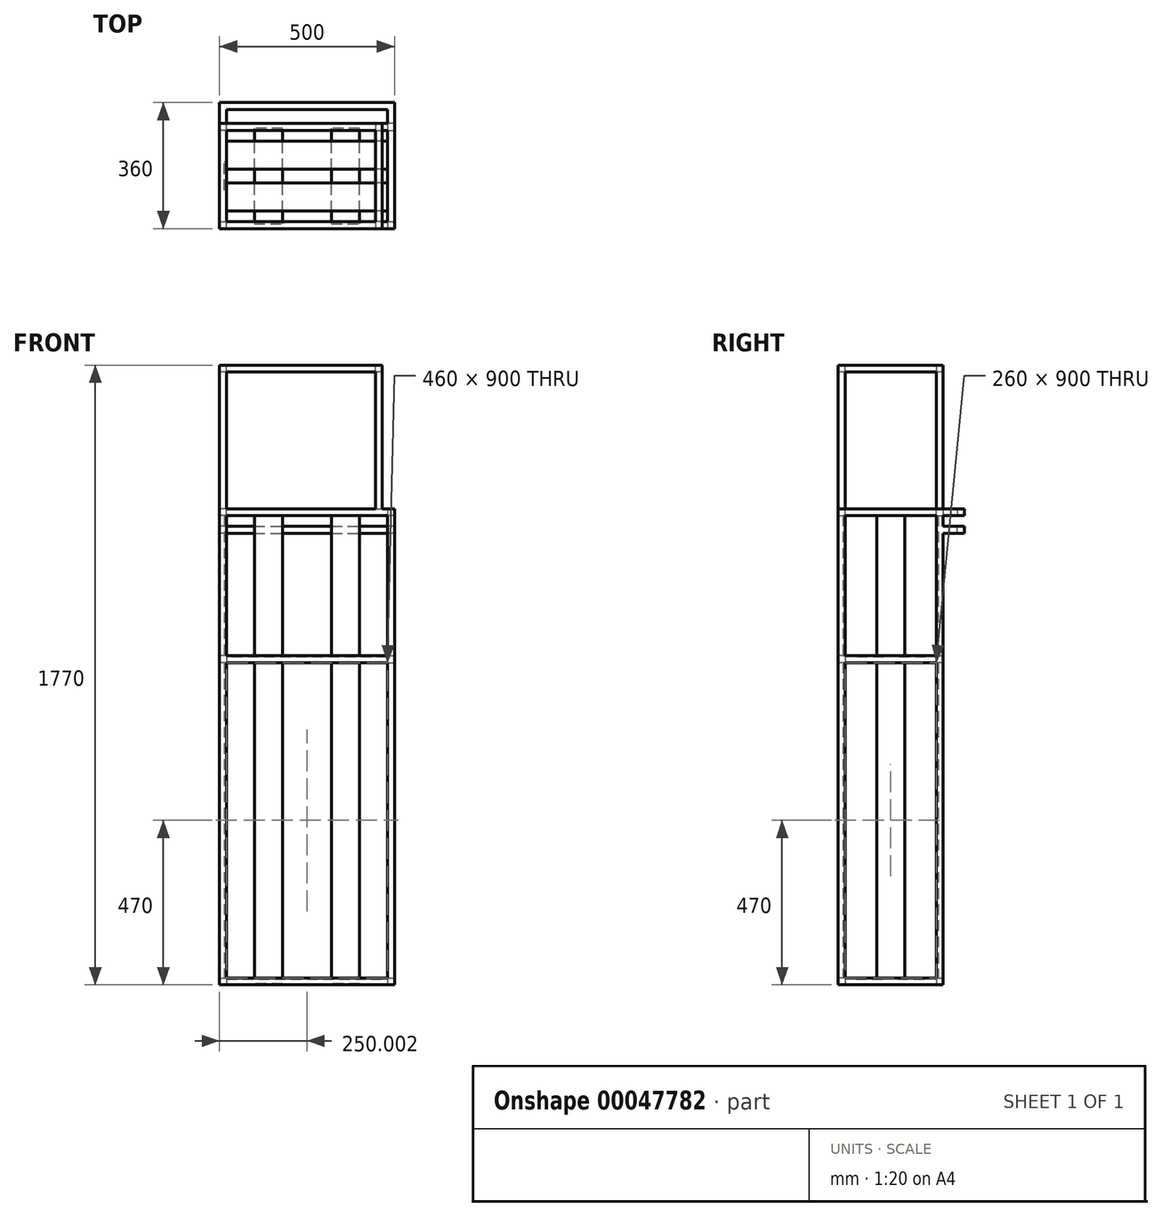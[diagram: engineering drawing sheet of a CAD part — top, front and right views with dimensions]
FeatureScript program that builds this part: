
annotation { "Feature Type Name" : "Feature", "Feature Type Description" : "" }
export const myFeature = defineFeature(function(context is Context, id is Id, definition is map)
    precondition{}
    {
        {
            var Q0;
            Q0=qCreatedBy(makeId("Top.planeOp"),FACE);
            var sketch = newSketch(context, id + "F0", { "sketchPlane" : qUnion([Q0])});
            skLineSegment(sketch, "E0.bottom", {"start": v(-269.64, 126.7) * mm, "end": v(230.36, 126.7) * mm});
            skLineSegment(sketch, "E0.top", {"start": v(-269.64, -173.3) * mm, "end": v(230.36, -173.3) * mm});
            skLineSegment(sketch, "E0.left", {"start": v(-269.64, 126.7) * mm, "end": v(-269.64, -173.3) * mm});
            skLineSegment(sketch, "E0.right", {"start": v(230.36, 126.7) * mm, "end": v(230.36, -173.3) * mm});
            skLineSegment(sketch, "E1.bottom", {"start": v(-249.64, 106.7) * mm, "end": v(210.36, 106.7) * mm});
            skLineSegment(sketch, "E1.top", {"start": v(-249.64, -153.3) * mm, "end": v(210.36, -153.3) * mm});
            skLineSegment(sketch, "E1.left", {"start": v(-249.64, 106.7) * mm, "end": v(-249.64, -153.3) * mm});
            skLineSegment(sketch, "E1.right", {"start": v(210.36, 106.7) * mm, "end": v(210.36, -153.3) * mm});
            skSolve(sketch);
        }
        {
            var Q0;
            Q0=makeQuery(id+"F0.imprint","IMPRINT",FACE,{"disambiguationData":[TD([[makeQuery(id+"F0.imprint","IMPRINT",EDGE,{"derivedFrom":sQuery(id+"F0.wireOp",EDGE,"E0.bottom")}),-1.0]])]});
            extrude(context, id + "F1", {"entities" : qUnion([Q0]), "depth" : 20 * mm});
        }
        {
            var Q0;
            Q0=makeQuery(id+"F1.opExtrude","SWEPT_FACE",FACE,{"disambiguationData":[OSD([sQuery(id+"F0.wireOp",EDGE,"E1.bottom")])]});
            var sketch = newSketch(context, id + "F2", { "sketchPlane" : qUnion([Q0])});
            skLineSegment(sketch, "E2.bottom", {"start": v(-169.64, 0) * mm, "end": v(-89.64, 0) * mm});
            skLineSegment(sketch, "E2.top", {"start": v(-169.64, 3) * mm, "end": v(-89.64, 3) * mm});
            skLineSegment(sketch, "E2.left", {"start": v(-169.64, 0) * mm, "end": v(-169.64, 3) * mm});
            skLineSegment(sketch, "E2.right", {"start": v(-89.64, 0) * mm, "end": v(-89.64, 3) * mm});
            skLineSegment(sketch, "E3.bottom", {"start": v(50.36, 3) * mm, "end": v(130.36, 3) * mm});
            skLineSegment(sketch, "E3.top", {"start": v(50.36, 0) * mm, "end": v(130.36, 0) * mm});
            skLineSegment(sketch, "E3.left", {"start": v(50.36, 3) * mm, "end": v(50.36, 0) * mm});
            skLineSegment(sketch, "E3.right", {"start": v(130.36, 3) * mm, "end": v(130.36, 0) * mm});
            skSolve(sketch);
        }
        {
            var Q0;
            Q0 = qSketchRegion(id + "F2", true);
            extrude(context, id + "F3", {"entities" : qUnion([Q0]), "operationType" : NewBodyOperationType.ADD, "endBound" : BoundingType.UP_TO_NEXT, "depth" : 25 * mm});
        }
        {
            var Q0;
            Q0=makeQuery(id+"F1.opExtrude","SWEPT_FACE",FACE,{"disambiguationData":[OSD([sQuery(id+"F0.wireOp",EDGE,"E1.right")])]});
            var sketch = newSketch(context, id + "F4", { "sketchPlane" : qUnion([Q0])});
            skLineSegment(sketch, "E4.bottom", {"start": v(-76.7, 20) * mm, "end": v(3.3, 20) * mm});
            skLineSegment(sketch, "E4.top", {"start": v(-76.7, 17) * mm, "end": v(3.3, 17) * mm});
            skLineSegment(sketch, "E4.left", {"start": v(-76.7, 20) * mm, "end": v(-76.7, 17) * mm});
            skLineSegment(sketch, "E4.right", {"start": v(3.3, 20) * mm, "end": v(3.3, 17) * mm});
            skLineSegment(sketch, "E5.bottom", {"start": v(43.3, 20) * mm, "end": v(123.3, 20) * mm});
            skLineSegment(sketch, "E5.top", {"start": v(43.3, 17) * mm, "end": v(123.3, 17) * mm});
            skLineSegment(sketch, "E5.left", {"start": v(43.3, 20) * mm, "end": v(43.3, 17) * mm});
            skLineSegment(sketch, "E5.right", {"start": v(123.3, 20) * mm, "end": v(123.3, 17) * mm});
            skSolve(sketch);
        }
        {
            var Q0;
            Q0 = qSketchRegion(id + "F4", true);
            extrude(context, id + "F5", {"entities" : qUnion([Q0]), "operationType" : NewBodyOperationType.ADD, "endBound" : BoundingType.UP_TO_NEXT, "depth" : 25 * mm});
        }
        {
            var Q0;
            Q0=makeQuery(id+"F5.boolean.opBoolean","MERGE",FACE,{"derivedFrom":[makeQuery(id+"F1.opExtrude","CAP_FACE",FACE,{"disambiguationData":[OSD([sQuery(id+"F0.wireOp",EDGE,"E0.bottom"),sQuery(id+"F0.wireOp",EDGE,"E0.top"),sQuery(id+"F0.wireOp",EDGE,"E0.left"),sQuery(id+"F0.wireOp",EDGE,"E0.right"),sQuery(id+"F0.wireOp",EDGE,"E1.bottom"),sQuery(id+"F0.wireOp",EDGE,"E1.top"),sQuery(id+"F0.wireOp",EDGE,"E1.left"),sQuery(id+"F0.wireOp",EDGE,"E1.right")])],"isStart":false}),makeQuery(id+"F5.opExtrude","SWEPT_FACE",FACE,{"disambiguationData":[OSD([sQuery(id+"F4.wireOp",EDGE,"E4.bottom")])]}),makeQuery(id+"F5.opExtrude","SWEPT_FACE",FACE,{"disambiguationData":[OSD([sQuery(id+"F4.wireOp",EDGE,"E5.bottom")])]})]});
            var sketch = newSketch(context, id + "F6", { "sketchPlane" : qUnion([Q0])});
            skLineSegment(sketch, "E6.bottom", {"start": v(-269.64, 126.7) * mm, "end": v(-249.64, 126.7) * mm});
            skLineSegment(sketch, "E6.top", {"start": v(-269.64, 106.7) * mm, "end": v(-249.64, 106.7) * mm});
            skLineSegment(sketch, "E6.left", {"start": v(-269.64, 126.7) * mm, "end": v(-269.64, 106.7) * mm});
            skLineSegment(sketch, "E6.right", {"start": v(-249.64, 126.7) * mm, "end": v(-249.64, 106.7) * mm});
            skLineSegment(sketch, "E7.bottom", {"start": v(-269.64, -173.3) * mm, "end": v(-249.64, -173.3) * mm});
            skLineSegment(sketch, "E7.top", {"start": v(-269.64, -153.3) * mm, "end": v(-249.64, -153.3) * mm});
            skLineSegment(sketch, "E7.left", {"start": v(-269.64, -173.3) * mm, "end": v(-269.64, -153.3) * mm});
            skLineSegment(sketch, "E7.right", {"start": v(-249.64, -173.3) * mm, "end": v(-249.64, -153.3) * mm});
            skLineSegment(sketch, "E8.bottom", {"start": v(210.36, -153.3) * mm, "end": v(230.36, -153.3) * mm});
            skLineSegment(sketch, "E8.top", {"start": v(210.36, -173.3) * mm, "end": v(230.36, -173.3) * mm});
            skLineSegment(sketch, "E8.left", {"start": v(210.36, -153.3) * mm, "end": v(210.36, -173.3) * mm});
            skLineSegment(sketch, "E8.right", {"start": v(230.36, -153.3) * mm, "end": v(230.36, -173.3) * mm});
            skLineSegment(sketch, "E9.bottom", {"start": v(210.36, 106.7) * mm, "end": v(230.36, 106.7) * mm});
            skLineSegment(sketch, "E9.top", {"start": v(210.36, 126.7) * mm, "end": v(230.36, 126.7) * mm});
            skLineSegment(sketch, "E9.left", {"start": v(210.36, 106.7) * mm, "end": v(210.36, 126.7) * mm});
            skLineSegment(sketch, "E9.right", {"start": v(230.36, 106.7) * mm, "end": v(230.36, 126.7) * mm});
            skSolve(sketch);
        }
        {
            var Q0;
            Q0 = qSketchRegion(id + "F6", true);
            extrude(context, id + "F7", {"entities" : qUnion([Q0]), "operationType" : NewBodyOperationType.ADD, "depth" : 1340 * mm});
        }
        {
            var Q0;
            Q0=makeQuery(id+"F7.opExtrude","SWEPT_FACE",FACE,{"disambiguationData":[OSD([sQuery(id+"F6.wireOp",EDGE,"E8.left")])]});
            var sketch = newSketch(context, id + "F8", { "sketchPlane" : qUnion([Q0])});
            skLineSegment(sketch, "E10.bottom", {"start": v(153.3, 920) * mm, "end": v(173.3, 920) * mm});
            skLineSegment(sketch, "E10.top", {"start": v(153.3, 940) * mm, "end": v(173.3, 940) * mm});
            skLineSegment(sketch, "E10.left", {"start": v(153.3, 940) * mm, "end": v(153.3, 920) * mm});
            skLineSegment(sketch, "E10.right", {"start": v(173.3, 940) * mm, "end": v(173.3, 920) * mm});
            skSolve(sketch);
        }
        {
            var Q0;
            Q0 = qSketchRegion(id + "F8", true);
            extrude(context, id + "F9", {"entities" : qUnion([Q0]), "operationType" : NewBodyOperationType.ADD, "endBound" : BoundingType.UP_TO_NEXT, "depth" : 25 * mm});
        }
        {
            var Q0;
            Q0=makeQuery(id+"F9.boolean.opBoolean","MERGE",FACE,{"derivedFrom":[makeQuery(id+"F7.opExtrude","SWEPT_FACE",FACE,{"disambiguationData":[OSD([sQuery(id+"F6.wireOp",EDGE,"E7.top")])]}),makeQuery(id+"F7.opExtrude","SWEPT_FACE",FACE,{"disambiguationData":[OSD([sQuery(id+"F6.wireOp",EDGE,"E8.bottom")])]}),makeQuery(id+"F9.opExtrude","SWEPT_FACE",FACE,{"disambiguationData":[OSD([sQuery(id+"F8.wireOp",EDGE,"E10.left")])]})]});
            var sketch = newSketch(context, id + "F10", { "sketchPlane" : qUnion([Q0])});
            skLineSegment(sketch, "E11.bottom", {"start": v(249.64, 940) * mm, "end": v(269.64, 940) * mm});
            skLineSegment(sketch, "E11.top", {"start": v(249.64, 920) * mm, "end": v(269.64, 920) * mm});
            skLineSegment(sketch, "E11.left", {"start": v(249.64, 940) * mm, "end": v(249.64, 920) * mm});
            skLineSegment(sketch, "E11.right", {"start": v(269.64, 940) * mm, "end": v(269.64, 920) * mm});
            skLineSegment(sketch, "E12.bottom", {"start": v(-210.36, 940) * mm, "end": v(-230.36, 940) * mm});
            skLineSegment(sketch, "E12.top", {"start": v(-210.36, 920) * mm, "end": v(-230.36, 920) * mm});
            skLineSegment(sketch, "E12.left", {"start": v(-210.36, 940) * mm, "end": v(-210.36, 920) * mm});
            skLineSegment(sketch, "E12.right", {"start": v(-230.36, 940) * mm, "end": v(-230.36, 920) * mm});
            skSolve(sketch);
        }
        {
            var Q0;
            Q0 = qSketchRegion(id + "F10", true);
            extrude(context, id + "F11", {"entities" : qUnion([Q0]), "operationType" : NewBodyOperationType.ADD, "endBound" : BoundingType.UP_TO_NEXT, "depth" : 25 * mm});
        }
        {
            var Q0;
            Q0=makeQuery(id+"F11.boolean.opBoolean","MERGE",FACE,{"derivedFrom":[makeQuery(id+"F7.opExtrude","SWEPT_FACE",FACE,{"disambiguationData":[OSD([sQuery(id+"F6.wireOp",EDGE,"E6.right")])]}),makeQuery(id+"F11.opExtrude","SWEPT_FACE",FACE,{"disambiguationData":[OSD([sQuery(id+"F10.wireOp",EDGE,"E11.left")])]})]});
            var sketch = newSketch(context, id + "F12", { "sketchPlane" : qUnion([Q0])});
            skLineSegment(sketch, "E13.bottom", {"start": v(106.7, 940) * mm, "end": v(126.7, 940) * mm});
            skLineSegment(sketch, "E13.top", {"start": v(106.7, 920) * mm, "end": v(126.7, 920) * mm});
            skLineSegment(sketch, "E13.left", {"start": v(106.7, 940) * mm, "end": v(106.7, 920) * mm});
            skLineSegment(sketch, "E13.right", {"start": v(126.7, 940) * mm, "end": v(126.7, 920) * mm});
            skSolve(sketch);
        }
        {
            var Q0;
            Q0 = qSketchRegion(id + "F12", true);
            extrude(context, id + "F13", {"entities" : qUnion([Q0]), "operationType" : NewBodyOperationType.ADD, "endBound" : BoundingType.UP_TO_NEXT, "depth" : 25 * mm});
        }
        {
            var Q0;
            {var subQ0=sQuery(id+"F0.wireOp",EDGE,"E0.left");var subQ1=sQuery(id+"F0.wireOp",EDGE,"E0.right");var subQ2=sQuery(id+"F0.wireOp",EDGE,"E1.bottom");var subQ3=sQuery(id+"F0.wireOp",EDGE,"E1.top");var subQ4=sQuery(id+"F0.wireOp",EDGE,"E1.left");var subQ5=sQuery(id+"F0.wireOp",EDGE,"E1.right");var subQ6=makeQuery(id+"F1.opExtrude","CAP_FACE",FACE,{"disambiguationData":[OSD([sQuery(id+"F0.wireOp",EDGE,"E0.bottom"),sQuery(id+"F0.wireOp",EDGE,"E0.top"),subQ0,subQ1,subQ2,subQ3,subQ4,subQ5])],"isStart":false});var subQ7=makeQuery(id+"F5.opExtrude","SWEPT_FACE",FACE,{"disambiguationData":[OSD([sQuery(id+"F4.wireOp",EDGE,"E4.bottom")])]});var subQ8=makeQuery(id+"F5.opExtrude","SWEPT_FACE",FACE,{"disambiguationData":[OSD([sQuery(id+"F4.wireOp",EDGE,"E5.bottom")])]});Q0=makeQuery(id+"F7.boolean.opBoolean","SPLIT",FACE,{"disambiguationData":[TD([makeQuery(id+"F1.opExtrude","SWEPT_FACE",FACE,{"disambiguationData":[OSD([subQ0])]})])],"derivedFrom":makeQuery(id+"F5.boolean.opBoolean","MERGE",FACE,{"derivedFrom":[subQ6,subQ7,subQ8]})});}
            var sketch = newSketch(context, id + "F14", { "sketchPlane" : qUnion([Q0])});
            skPoint(sketch, "E14", {"position": v(-269.64, -23.3) * mm});
            skLineSegment(sketch, "E15.bottom", {"start": v(-252.64, -63.3) * mm, "end": v(-255.64, -63.3) * mm});
            skLineSegment(sketch, "E15.top", {"start": v(-252.64, 16.7) * mm, "end": v(-255.64, 16.7) * mm});
            skLineSegment(sketch, "E15.left", {"start": v(-252.64, -63.3) * mm, "end": v(-252.64, 16.7) * mm});
            skLineSegment(sketch, "E15.right", {"start": v(-255.64, -63.3) * mm, "end": v(-255.64, 16.7) * mm});
            skSolve(sketch);
        }
        {
            var Q0;
            Q0 = qSketchRegion(id + "F14", true);
            extrude(context, id + "F15", {"entities" : qUnion([Q0]), "operationType" : NewBodyOperationType.ADD, "endBound" : BoundingType.UP_TO_NEXT, "depth" : 25 * mm});
        }
        {
            var Q0;
            {var subQ0=sQuery(id+"F0.wireOp",EDGE,"E0.bottom");var subQ1=sQuery(id+"F0.wireOp",EDGE,"E1.bottom");var subQ2=sQuery(id+"F0.wireOp",EDGE,"E1.left");var subQ3=sQuery(id+"F0.wireOp",EDGE,"E1.right");var subQ4=makeQuery(id+"F1.opExtrude","CAP_FACE",FACE,{"disambiguationData":[OSD([subQ0,sQuery(id+"F0.wireOp",EDGE,"E0.top"),sQuery(id+"F0.wireOp",EDGE,"E0.left"),sQuery(id+"F0.wireOp",EDGE,"E0.right"),subQ1,sQuery(id+"F0.wireOp",EDGE,"E1.top"),subQ2,subQ3])],"isStart":false});var subQ5=makeQuery(id+"F5.opExtrude","SWEPT_FACE",FACE,{"disambiguationData":[OSD([sQuery(id+"F4.wireOp",EDGE,"E4.bottom")])]});var subQ6=makeQuery(id+"F5.opExtrude","SWEPT_FACE",FACE,{"disambiguationData":[OSD([sQuery(id+"F4.wireOp",EDGE,"E5.bottom")])]});Q0=makeQuery(id+"F7.boolean.opBoolean","SPLIT",FACE,{"disambiguationData":[TD([makeQuery(id+"F1.opExtrude","SWEPT_FACE",FACE,{"disambiguationData":[OSD([subQ0])]})])],"derivedFrom":makeQuery(id+"F5.boolean.opBoolean","MERGE",FACE,{"derivedFrom":[subQ4,subQ5,subQ6]})});}
            var sketch = newSketch(context, id + "F16", { "sketchPlane" : qUnion([Q0])});
            skLineSegment(sketch, "E16.bottom", {"start": v(130.36, 109.7) * mm, "end": v(50.36, 109.7) * mm});
            skLineSegment(sketch, "E16.top", {"start": v(130.36, 112.7) * mm, "end": v(50.36, 112.7) * mm});
            skLineSegment(sketch, "E16.left", {"start": v(130.36, 109.7) * mm, "end": v(130.36, 112.7) * mm});
            skLineSegment(sketch, "E16.right", {"start": v(50.36, 109.7) * mm, "end": v(50.36, 112.7) * mm});
            skLineSegment(sketch, "E17.bottom", {"start": v(-89.64, 109.7) * mm, "end": v(-169.64, 109.7) * mm});
            skLineSegment(sketch, "E17.top", {"start": v(-89.64, 112.7) * mm, "end": v(-169.64, 112.7) * mm});
            skLineSegment(sketch, "E17.left", {"start": v(-89.64, 109.7) * mm, "end": v(-89.64, 112.7) * mm});
            skLineSegment(sketch, "E17.right", {"start": v(-169.64, 109.7) * mm, "end": v(-169.64, 112.7) * mm});
            skSolve(sketch);
        }
        {
            var Q0;
            Q0 = qSketchRegion(id + "F16", true);
            extrude(context, id + "F17", {"entities" : qUnion([Q0]), "operationType" : NewBodyOperationType.ADD, "endBound" : BoundingType.UP_TO_NEXT, "depth" : 25 * mm});
        }
        {
            var Q0;
            {var subQ0=sQuery(id+"F0.wireOp",EDGE,"E0.top");var subQ1=sQuery(id+"F0.wireOp",EDGE,"E1.top");var subQ2=sQuery(id+"F0.wireOp",EDGE,"E1.left");var subQ3=sQuery(id+"F0.wireOp",EDGE,"E1.right");var subQ4=makeQuery(id+"F1.opExtrude","CAP_FACE",FACE,{"disambiguationData":[OSD([sQuery(id+"F0.wireOp",EDGE,"E0.bottom"),subQ0,sQuery(id+"F0.wireOp",EDGE,"E0.left"),sQuery(id+"F0.wireOp",EDGE,"E0.right"),sQuery(id+"F0.wireOp",EDGE,"E1.bottom"),subQ1,subQ2,subQ3])],"isStart":false});var subQ5=makeQuery(id+"F5.opExtrude","SWEPT_FACE",FACE,{"disambiguationData":[OSD([sQuery(id+"F4.wireOp",EDGE,"E4.bottom")])]});var subQ6=makeQuery(id+"F5.opExtrude","SWEPT_FACE",FACE,{"disambiguationData":[OSD([sQuery(id+"F4.wireOp",EDGE,"E5.bottom")])]});Q0=makeQuery(id+"F7.boolean.opBoolean","SPLIT",FACE,{"disambiguationData":[TD([makeQuery(id+"F1.opExtrude","SWEPT_FACE",FACE,{"disambiguationData":[OSD([subQ0])]})])],"derivedFrom":makeQuery(id+"F5.boolean.opBoolean","MERGE",FACE,{"derivedFrom":[subQ4,subQ5,subQ6]})});}
            var sketch = newSketch(context, id + "F18", { "sketchPlane" : qUnion([Q0])});
            skLineSegment(sketch, "E18.bottom", {"start": v(-169.64, -156.3) * mm, "end": v(-89.64, -156.3) * mm});
            skLineSegment(sketch, "E18.top", {"start": v(-169.64, -159.3) * mm, "end": v(-89.64, -159.3) * mm});
            skLineSegment(sketch, "E18.left", {"start": v(-169.64, -156.3) * mm, "end": v(-169.64, -159.3) * mm});
            skLineSegment(sketch, "E18.right", {"start": v(-89.64, -156.3) * mm, "end": v(-89.64, -159.3) * mm});
            skLineSegment(sketch, "E19.bottom", {"start": v(50.36, -156.3) * mm, "end": v(130.36, -156.3) * mm});
            skLineSegment(sketch, "E19.top", {"start": v(50.36, -159.3) * mm, "end": v(130.36, -159.3) * mm});
            skLineSegment(sketch, "E19.left", {"start": v(50.36, -156.3) * mm, "end": v(50.36, -159.3) * mm});
            skLineSegment(sketch, "E19.right", {"start": v(130.36, -156.3) * mm, "end": v(130.36, -159.3) * mm});
            skSolve(sketch);
        }
        {
            var Q0;
            Q0 = qSketchRegion(id + "F18", true);
            extrude(context, id + "F19", {"entities" : qUnion([Q0]), "operationType" : NewBodyOperationType.ADD, "endBound" : BoundingType.UP_TO_NEXT, "depth" : 25 * mm});
        }
        {
            var Q0;
            {var subQ0=sQuery(id+"F6.wireOp",EDGE,"E8.left");Q0=makeQuery(id+"F9.boolean.opBoolean","SPLIT",FACE,{"disambiguationData":[TD([makeQuery(id+"F9.opExtrude","SWEPT_FACE",FACE,{"disambiguationData":[OSD([sQuery(id+"F8.wireOp",EDGE,"E10.top")])]})])],"derivedFrom":makeQuery(id+"F7.opExtrude","SWEPT_FACE",FACE,{"disambiguationData":[OSD([subQ0])]})});}
            var sketch = newSketch(context, id + "F20", { "sketchPlane" : qUnion([Q0])});
            skLineSegment(sketch, "E20.bottom", {"start": v(173.3, 1360) * mm, "end": v(153.3, 1360) * mm});
            skLineSegment(sketch, "E20.top", {"start": v(173.3, 1340) * mm, "end": v(153.3, 1340) * mm});
            skLineSegment(sketch, "E20.left", {"start": v(173.3, 1360) * mm, "end": v(173.3, 1340) * mm});
            skLineSegment(sketch, "E20.right", {"start": v(153.3, 1360) * mm, "end": v(153.3, 1340) * mm});
            skSolve(sketch);
        }
        {
            var Q0;
            Q0 = qSketchRegion(id + "F20", true);
            extrude(context, id + "F21", {"entities" : qUnion([Q0]), "operationType" : NewBodyOperationType.ADD, "endBound" : BoundingType.UP_TO_NEXT, "depth" : 25 * mm});
        }
        {
            var Q0;
            {var subQ0=sQuery(id+"F6.wireOp",EDGE,"E7.top");var subQ1=makeQuery(id+"F7.opExtrude","SWEPT_FACE",FACE,{"disambiguationData":[OSD([subQ0])]});var subQ2=sQuery(id+"F6.wireOp",EDGE,"E8.bottom");var subQ3=makeQuery(id+"F7.opExtrude","SWEPT_FACE",FACE,{"disambiguationData":[OSD([subQ2])]});var subQ4=makeQuery(id+"F9.opExtrude","SWEPT_FACE",FACE,{"disambiguationData":[OSD([sQuery(id+"F8.wireOp",EDGE,"E10.left")])]});var subQ5=makeQuery(id+"F9.boolean.opBoolean","MERGE",FACE,{"derivedFrom":[subQ1,subQ3,subQ4]});var subQ6=sQuery(id+"F6.wireOp",EDGE,"E7.left");var subQ7=sQuery(id+"F6.wireOp",EDGE,"E7.right");var subQ8=makeQuery(id+"F9.opExtrude","SWEPT_FACE",FACE,{"disambiguationData":[OSD([sQuery(id+"F8.wireOp",EDGE,"E10.top")])]});var subQ9=sQuery(id+"F6.wireOp",EDGE,"E8.left");var subQ10=sQuery(id+"F6.wireOp",EDGE,"E8.right");Q0=makeQuery(id+"F21.boolean.opBoolean","MERGE",FACE,{"derivedFrom":[makeQuery(id+"F11.boolean.opBoolean","SPLIT",FACE,{"disambiguationData":[TD([makeQuery(id+"F1.opExtrude","SWEPT_FACE",FACE,{"disambiguationData":[OSD([sQuery(id+"F0.wireOp",EDGE,"E0.left")])]}),makeQuery(id+"F7.opExtrude","SWEPT_FACE",FACE,{"disambiguationData":[OSD([sQuery(id+"F6.wireOp",EDGE,"E6.left")])]}),makeQuery(id+"F7.opExtrude","SWEPT_FACE",FACE,{"disambiguationData":[OSD([sQuery(id+"F6.wireOp",EDGE,"E6.right")])]}),makeQuery(id+"F7.opExtrude","CAP_FACE",FACE,{"disambiguationData":[OSD([sQuery(id+"F6.wireOp",EDGE,"E7.bottom"),subQ0,subQ6,subQ7])],"isStart":false}),subQ1,makeQuery(id+"F7.opExtrude","SWEPT_FACE",FACE,{"disambiguationData":[OSD([subQ6])]}),makeQuery(id+"F7.opExtrude","SWEPT_FACE",FACE,{"disambiguationData":[OSD([subQ7])]}),subQ3,subQ8,subQ4,makeQuery(id+"F11.opExtrude","SWEPT_FACE",FACE,{"disambiguationData":[OSD([sQuery(id+"F10.wireOp",EDGE,"E11.bottom")])]}),makeQuery(id+"F11.opExtrude","SWEPT_FACE",FACE,{"disambiguationData":[OSD([sQuery(id+"F10.wireOp",EDGE,"E11.left")])]}),makeQuery(id+"F11.opExtrude","SWEPT_FACE",FACE,{"disambiguationData":[OSD([sQuery(id+"F10.wireOp",EDGE,"E11.right")])]})])],"derivedFrom":subQ5}),makeQuery(id+"F11.boolean.opBoolean","SPLIT",FACE,{"disambiguationData":[TD([makeQuery(id+"F1.opExtrude","SWEPT_FACE",FACE,{"disambiguationData":[OSD([sQuery(id+"F0.wireOp",EDGE,"E0.right")])]}),subQ1,subQ3,makeQuery(id+"F7.opExtrude","CAP_FACE",FACE,{"disambiguationData":[OSD([subQ2,sQuery(id+"F6.wireOp",EDGE,"E8.top"),subQ9,subQ10])],"isStart":false}),makeQuery(id+"F7.opExtrude","SWEPT_FACE",FACE,{"disambiguationData":[OSD([subQ9])]}),makeQuery(id+"F7.opExtrude","SWEPT_FACE",FACE,{"disambiguationData":[OSD([subQ10])]}),makeQuery(id+"F7.opExtrude","SWEPT_FACE",FACE,{"disambiguationData":[OSD([sQuery(id+"F6.wireOp",EDGE,"E9.left")])]}),makeQuery(id+"F7.opExtrude","SWEPT_FACE",FACE,{"disambiguationData":[OSD([sQuery(id+"F6.wireOp",EDGE,"E9.right")])]}),subQ8,subQ4,makeQuery(id+"F11.opExtrude","SWEPT_FACE",FACE,{"disambiguationData":[OSD([sQuery(id+"F10.wireOp",EDGE,"E12.bottom")])]}),makeQuery(id+"F11.opExtrude","SWEPT_FACE",FACE,{"disambiguationData":[OSD([sQuery(id+"F10.wireOp",EDGE,"E12.left")])]}),makeQuery(id+"F11.opExtrude","SWEPT_FACE",FACE,{"disambiguationData":[OSD([sQuery(id+"F10.wireOp",EDGE,"E12.right")])]})])],"derivedFrom":subQ5}),makeQuery(id+"F21.opExtrude","SWEPT_FACE",FACE,{"disambiguationData":[OSD([sQuery(id+"F20.wireOp",EDGE,"E20.right")])]})]});}
            var sketch = newSketch(context, id + "F22", { "sketchPlane" : qUnion([Q0])});
            skLineSegment(sketch, "E21.bottom", {"start": v(-230.36, 1360) * mm, "end": v(-210.36, 1360) * mm});
            skLineSegment(sketch, "E21.top", {"start": v(-230.36, 1340) * mm, "end": v(-210.36, 1340) * mm});
            skLineSegment(sketch, "E21.left", {"start": v(-230.36, 1360) * mm, "end": v(-230.36, 1340) * mm});
            skLineSegment(sketch, "E21.right", {"start": v(-210.36, 1360) * mm, "end": v(-210.36, 1340) * mm});
            skLineSegment(sketch, "E22.bottom", {"start": v(249.64, 1340) * mm, "end": v(269.64, 1340) * mm});
            skLineSegment(sketch, "E22.top", {"start": v(249.64, 1360) * mm, "end": v(269.64, 1360) * mm});
            skLineSegment(sketch, "E22.left", {"start": v(249.64, 1340) * mm, "end": v(249.64, 1360) * mm});
            skLineSegment(sketch, "E22.right", {"start": v(269.64, 1340) * mm, "end": v(269.64, 1360) * mm});
            skSolve(sketch);
        }
        {
            var Q0;
            Q0 = qSketchRegion(id + "F22", true);
            extrude(context, id + "F23", {"entities" : qUnion([Q0]), "operationType" : NewBodyOperationType.ADD, "endBound" : BoundingType.UP_TO_NEXT, "depth" : 25 * mm});
        }
        {
            var Q0;
            {var subQ0=sQuery(id+"F6.wireOp",EDGE,"E9.left");var subQ1=makeQuery(id+"F7.opExtrude","SWEPT_FACE",FACE,{"disambiguationData":[OSD([subQ0])]});var subQ2=makeQuery(id+"F11.opExtrude","SWEPT_FACE",FACE,{"disambiguationData":[OSD([sQuery(id+"F10.wireOp",EDGE,"E12.left")])]});var subQ3=sQuery(id+"F6.wireOp",EDGE,"E9.bottom");var subQ4=sQuery(id+"F6.wireOp",EDGE,"E9.top");Q0=makeQuery(id+"F23.boolean.opBoolean","MERGE",FACE,{"derivedFrom":[makeQuery(id+"F13.boolean.opBoolean","SPLIT",FACE,{"disambiguationData":[TD([makeQuery(id+"F7.opExtrude","CAP_FACE",FACE,{"disambiguationData":[OSD([subQ3,subQ4,subQ0,sQuery(id+"F6.wireOp",EDGE,"E9.right")])],"isStart":false})])],"derivedFrom":makeQuery(id+"F11.boolean.opBoolean","MERGE",FACE,{"derivedFrom":[subQ1,subQ2]})}),makeQuery(id+"F23.opExtrude","SWEPT_FACE",FACE,{"disambiguationData":[OSD([sQuery(id+"F22.wireOp",EDGE,"E21.right")])]})]});}
            var sketch = newSketch(context, id + "F24", { "sketchPlane" : qUnion([Q0])});
            skLineSegment(sketch, "E23.bottom", {"start": v(-126.7, 1360) * mm, "end": v(-106.7, 1360) * mm});
            skLineSegment(sketch, "E23.top", {"start": v(-126.7, 1340) * mm, "end": v(-106.7, 1340) * mm});
            skLineSegment(sketch, "E23.left", {"start": v(-126.7, 1360) * mm, "end": v(-126.7, 1340) * mm});
            skLineSegment(sketch, "E23.right", {"start": v(-106.7, 1360) * mm, "end": v(-106.7, 1340) * mm});
            skSolve(sketch);
        }
        {
            var Q0;
            Q0 = qSketchRegion(id + "F24", true);
            extrude(context, id + "F25", {"entities" : qUnion([Q0]), "operationType" : NewBodyOperationType.ADD, "endBound" : BoundingType.UP_TO_NEXT, "depth" : 25 * mm});
        }
        {
            var Q0;
            {var subQ0=makeQuery(id+"F7.opExtrude","SWEPT_FACE",FACE,{"disambiguationData":[OSD([sQuery(id+"F6.wireOp",EDGE,"E6.right")])]});var subQ1=makeQuery(id+"F11.opExtrude","SWEPT_FACE",FACE,{"disambiguationData":[OSD([sQuery(id+"F10.wireOp",EDGE,"E11.left")])]});Q0=makeQuery(id+"F13.boolean.opBoolean","SPLIT",FACE,{"disambiguationData":[TD([makeQuery(id+"F7.opExtrude","SWEPT_FACE",FACE,{"disambiguationData":[OSD([sQuery(id+"F6.wireOp",EDGE,"E7.top")])]})])],"derivedFrom":makeQuery(id+"F11.boolean.opBoolean","MERGE",FACE,{"derivedFrom":[subQ0,subQ1]})});}
            var sketch = newSketch(context, id + "F26", { "sketchPlane" : qUnion([Q0])});
            skLineSegment(sketch, "E24.bottom", {"start": v(-123.3, 940) * mm, "end": v(-43.3, 940) * mm});
            skLineSegment(sketch, "E24.top", {"start": v(-123.3, 937) * mm, "end": v(-43.3, 937) * mm});
            skLineSegment(sketch, "E24.left", {"start": v(-123.3, 940) * mm, "end": v(-123.3, 937) * mm});
            skLineSegment(sketch, "E24.right", {"start": v(-43.3, 940) * mm, "end": v(-43.3, 937) * mm});
            skLineSegment(sketch, "E25.bottom", {"start": v(-3.3, 940) * mm, "end": v(76.7, 940) * mm});
            skLineSegment(sketch, "E25.top", {"start": v(-3.3, 937) * mm, "end": v(76.7, 937) * mm});
            skLineSegment(sketch, "E25.left", {"start": v(-3.3, 940) * mm, "end": v(-3.3, 937) * mm});
            skLineSegment(sketch, "E25.right", {"start": v(76.7, 940) * mm, "end": v(76.7, 937) * mm});
            skSolve(sketch);
        }
        {
            var Q0;
            Q0 = qSketchRegion(id + "F26", true);
            extrude(context, id + "F27", {"entities" : qUnion([Q0]), "operationType" : NewBodyOperationType.ADD, "endBound" : BoundingType.UP_TO_NEXT, "depth" : 25 * mm});
        }
        {
            var Q0;
            Q0=makeQuery(id+"F27.boolean.opBoolean","MERGE",FACE,{"derivedFrom":[makeQuery(id+"F11.opExtrude","SWEPT_FACE",FACE,{"disambiguationData":[OSD([sQuery(id+"F10.wireOp",EDGE,"E11.bottom")])]}),makeQuery(id+"F11.opExtrude","SWEPT_FACE",FACE,{"disambiguationData":[OSD([sQuery(id+"F10.wireOp",EDGE,"E12.bottom")])]}),makeQuery(id+"F27.opExtrude","SWEPT_FACE",FACE,{"disambiguationData":[OSD([sQuery(id+"F26.wireOp",EDGE,"E24.bottom")])]}),makeQuery(id+"F27.opExtrude","SWEPT_FACE",FACE,{"disambiguationData":[OSD([sQuery(id+"F26.wireOp",EDGE,"E25.bottom")])]})]});
            var sketch = newSketch(context, id + "F28", { "sketchPlane" : qUnion([Q0])});
            skPoint(sketch, "E26", {"position": v(-269.64, -23.3) * mm});
            skLineSegment(sketch, "E27.bottom", {"start": v(-252.64, -63.3) * mm, "end": v(-255.64, -63.3) * mm});
            skLineSegment(sketch, "E27.top", {"start": v(-252.64, 16.7) * mm, "end": v(-255.64, 16.7) * mm});
            skLineSegment(sketch, "E27.left", {"start": v(-252.64, -63.3) * mm, "end": v(-252.64, 16.7) * mm});
            skLineSegment(sketch, "E27.right", {"start": v(-255.64, -63.3) * mm, "end": v(-255.64, 16.7) * mm});
            skSolve(sketch);
        }
        {
            var Q0;
            Q0 = qSketchRegion(id + "F28", true);
            extrude(context, id + "F29", {"entities" : qUnion([Q0]), "operationType" : NewBodyOperationType.ADD, "endBound" : BoundingType.UP_TO_NEXT, "depth" : 25 * mm});
        }
        {
            var Q0;
            Q0=makeQuery(id+"F9.opExtrude","SWEPT_FACE",FACE,{"disambiguationData":[OSD([sQuery(id+"F8.wireOp",EDGE,"E10.top")])]});
            var sketch = newSketch(context, id + "F30", { "sketchPlane" : qUnion([Q0])});
            skLineSegment(sketch, "E28.bottom", {"start": v(130.36, -159.3) * mm, "end": v(50.36, -159.3) * mm});
            skLineSegment(sketch, "E28.top", {"start": v(130.36, -156.3) * mm, "end": v(50.36, -156.3) * mm});
            skLineSegment(sketch, "E28.left", {"start": v(130.36, -159.3) * mm, "end": v(130.36, -156.3) * mm});
            skLineSegment(sketch, "E28.right", {"start": v(50.36, -159.3) * mm, "end": v(50.36, -156.3) * mm});
            skLineSegment(sketch, "E29.bottom", {"start": v(-89.64, -159.3) * mm, "end": v(-169.64, -159.3) * mm});
            skLineSegment(sketch, "E29.top", {"start": v(-89.64, -156.3) * mm, "end": v(-169.64, -156.3) * mm});
            skLineSegment(sketch, "E29.left", {"start": v(-89.64, -159.3) * mm, "end": v(-89.64, -156.3) * mm});
            skLineSegment(sketch, "E29.right", {"start": v(-169.64, -159.3) * mm, "end": v(-169.64, -156.3) * mm});
            skSolve(sketch);
        }
        {
            var Q0;
            Q0 = qSketchRegion(id + "F30", true);
            extrude(context, id + "F31", {"entities" : qUnion([Q0]), "operationType" : NewBodyOperationType.ADD, "endBound" : BoundingType.UP_TO_NEXT, "depth" : 25 * mm});
        }
        {
            var Q0;
            Q0=makeQuery(id+"F13.opExtrude","SWEPT_FACE",FACE,{"disambiguationData":[OSD([sQuery(id+"F12.wireOp",EDGE,"E13.bottom")])]});
            var sketch = newSketch(context, id + "F32", { "sketchPlane" : qUnion([Q0])});
            skLineSegment(sketch, "E30.bottom", {"start": v(130.36, 109.7) * mm, "end": v(50.36, 109.7) * mm});
            skLineSegment(sketch, "E30.top", {"start": v(130.36, 112.7) * mm, "end": v(50.36, 112.7) * mm});
            skLineSegment(sketch, "E30.left", {"start": v(130.36, 109.7) * mm, "end": v(130.36, 112.7) * mm});
            skLineSegment(sketch, "E30.right", {"start": v(50.36, 109.7) * mm, "end": v(50.36, 112.7) * mm});
            skLineSegment(sketch, "E31.bottom", {"start": v(-89.64, 109.7) * mm, "end": v(-169.64, 109.7) * mm});
            skLineSegment(sketch, "E31.top", {"start": v(-89.64, 112.7) * mm, "end": v(-169.64, 112.7) * mm});
            skLineSegment(sketch, "E31.left", {"start": v(-89.64, 109.7) * mm, "end": v(-89.64, 112.7) * mm});
            skLineSegment(sketch, "E31.right", {"start": v(-169.64, 109.7) * mm, "end": v(-169.64, 112.7) * mm});
            skSolve(sketch);
        }
        {
            var Q0;
            Q0 = qSketchRegion(id + "F32", true);
            extrude(context, id + "F33", {"entities" : qUnion([Q0]), "operationType" : NewBodyOperationType.ADD, "endBound" : BoundingType.UP_TO_NEXT, "depth" : 25 * mm});
        }
        {
            var Q0;
            Q0=makeQuery(id+"F25.boolean.opBoolean","MERGE",FACE,{"derivedFrom":[makeQuery(id+"F13.boolean.opBoolean","MERGE",FACE,{"derivedFrom":[makeQuery(id+"F7.boolean.opBoolean","MERGE",FACE,{"derivedFrom":[makeQuery(id+"F1.opExtrude","SWEPT_FACE",FACE,{"disambiguationData":[OSD([sQuery(id+"F0.wireOp",EDGE,"E0.bottom")])]}),makeQuery(id+"F7.opExtrude","SWEPT_FACE",FACE,{"disambiguationData":[OSD([sQuery(id+"F6.wireOp",EDGE,"E6.bottom")])]}),makeQuery(id+"F7.opExtrude","SWEPT_FACE",FACE,{"disambiguationData":[OSD([sQuery(id+"F6.wireOp",EDGE,"E9.top")])]})]}),makeQuery(id+"F13.opExtrude","SWEPT_FACE",FACE,{"disambiguationData":[OSD([sQuery(id+"F12.wireOp",EDGE,"E13.right")])]})]}),makeQuery(id+"F25.opExtrude","SWEPT_FACE",FACE,{"disambiguationData":[OSD([sQuery(id+"F24.wireOp",EDGE,"E23.left")])]})]});
            var sketch = newSketch(context, id + "F34", { "sketchPlane" : qUnion([Q0])});
            skLineSegment(sketch, "E32.bottom", {"start": v(-230.36, 1360) * mm, "end": v(-210.36, 1360) * mm});
            skLineSegment(sketch, "E32.top", {"start": v(-230.36, 1340) * mm, "end": v(-210.36, 1340) * mm});
            skLineSegment(sketch, "E32.left", {"start": v(-230.36, 1360) * mm, "end": v(-230.36, 1340) * mm});
            skLineSegment(sketch, "E32.right", {"start": v(-210.36, 1360) * mm, "end": v(-210.36, 1340) * mm});
            skLineSegment(sketch, "E33.bottom", {"start": v(249.64, 1340) * mm, "end": v(269.64, 1340) * mm});
            skLineSegment(sketch, "E33.top", {"start": v(249.64, 1360) * mm, "end": v(269.64, 1360) * mm});
            skLineSegment(sketch, "E33.left", {"start": v(249.64, 1340) * mm, "end": v(249.64, 1360) * mm});
            skLineSegment(sketch, "E33.right", {"start": v(269.64, 1340) * mm, "end": v(269.64, 1360) * mm});
            skLineSegment(sketch, "E34.bottom", {"start": v(-230.36, 1310) * mm, "end": v(-210.36, 1310) * mm});
            skLineSegment(sketch, "E34.top", {"start": v(-230.36, 1290) * mm, "end": v(-210.36, 1290) * mm});
            skLineSegment(sketch, "E34.left", {"start": v(-230.36, 1310) * mm, "end": v(-230.36, 1290) * mm});
            skLineSegment(sketch, "E34.right", {"start": v(-210.36, 1310) * mm, "end": v(-210.36, 1290) * mm});
            skLineSegment(sketch, "E35.bottom", {"start": v(249.64, 1310) * mm, "end": v(269.64, 1310) * mm});
            skLineSegment(sketch, "E35.top", {"start": v(249.64, 1290) * mm, "end": v(269.64, 1290) * mm});
            skLineSegment(sketch, "E35.left", {"start": v(249.64, 1310) * mm, "end": v(249.64, 1290) * mm});
            skLineSegment(sketch, "E35.right", {"start": v(269.64, 1310) * mm, "end": v(269.64, 1290) * mm});
            skSolve(sketch);
        }
        {
            var Q0;
            Q0 = qSketchRegion(id + "F34", true);
            extrude(context, id + "F35", {"entities" : qUnion([Q0]), "operationType" : NewBodyOperationType.ADD, "depth" : 60 * mm});
        }
        {
            var Q0;
            {var subQ0=sQuery(id+"F6.wireOp",EDGE,"E9.left");var subQ1=makeQuery(id+"F7.opExtrude","SWEPT_FACE",FACE,{"disambiguationData":[OSD([subQ0])]});var subQ2=makeQuery(id+"F11.opExtrude","SWEPT_FACE",FACE,{"disambiguationData":[OSD([sQuery(id+"F10.wireOp",EDGE,"E12.left")])]});var subQ4=sQuery(id+"F6.wireOp",EDGE,"E9.bottom");var subQ5=sQuery(id+"F6.wireOp",EDGE,"E9.top");var subQ6=makeQuery(id+"F1.opExtrude","SWEPT_FACE",FACE,{"disambiguationData":[OSD([sQuery(id+"F0.wireOp",EDGE,"E0.bottom")])]});var subQ13=makeQuery(id+"F23.opExtrude","SWEPT_FACE",FACE,{"disambiguationData":[OSD([sQuery(id+"F22.wireOp",EDGE,"E21.right")])]});Q0=makeQuery(id+"F4ijyKHvJpF9RY2_1.boolean.opBoolean","MERGE",FACE,{"derivedFrom":[makeQuery(id+"F35.opExtrude","SWEPT_FACE",FACE,{"disambiguationData":[OSD([sQuery(id+"F34.wireOp",EDGE,"E32.right")])]}),makeQuery(id+"F35.boolean.opBoolean","MERGE",FACE,{"derivedFrom":[makeQuery(id+"F25.boolean.opBoolean","SPLIT",FACE,{"disambiguationData":[TD([subQ6])],"derivedFrom":makeQuery(id+"F23.boolean.opBoolean","MERGE",FACE,{"derivedFrom":[makeQuery(id+"F13.boolean.opBoolean","SPLIT",FACE,{"disambiguationData":[TD([makeQuery(id+"F7.opExtrude","CAP_FACE",FACE,{"disambiguationData":[OSD([subQ4,subQ5,subQ0,sQuery(id+"F6.wireOp",EDGE,"E9.right")])],"isStart":false})])],"derivedFrom":makeQuery(id+"F11.boolean.opBoolean","MERGE",FACE,{"derivedFrom":[subQ1,subQ2]})}),subQ13]})}),makeQuery(id+"F35.opExtrude","SWEPT_FACE",FACE,{"disambiguationData":[OSD([sQuery(id+"F34.wireOp",EDGE,"E34.right")])]})]}),makeQuery(id+"F4ijyKHvJpF9RY2_1.opExtrude","SWEPT_FACE",FACE,{"disambiguationData":[OSD([sQuery(id+"Fg5j8f6UDMg1IWg_1.wireOp",EDGE,"d46cd931-0203-4b11-a075-3bcfa34f269a.left")])]})]});}
            var sketch = newSketch(context, id + "F36", { "sketchPlane" : qUnion([Q0])});
            skLineSegment(sketch, "E36.bottom", {"start": v(-186.7, 1360) * mm, "end": v(-166.7, 1360) * mm});
            skLineSegment(sketch, "E36.top", {"start": v(-186.7, 1340) * mm, "end": v(-166.7, 1340) * mm});
            skLineSegment(sketch, "E36.left", {"start": v(-186.7, 1360) * mm, "end": v(-186.7, 1340) * mm});
            skLineSegment(sketch, "E36.right", {"start": v(-166.7, 1360) * mm, "end": v(-166.7, 1340) * mm});
            skSolve(sketch);
        }
        {
            var Q0;
            Q0 = qSketchRegion(id + "F36", true);
            extrude(context, id + "F37", {"entities" : qUnion([Q0]), "operationType" : NewBodyOperationType.ADD, "endBound" : BoundingType.UP_TO_NEXT, "depth" : 25 * mm});
        }
        {
            var Q0;
            Q0=makeQuery(id+"F37.boolean.opBoolean","MERGE",FACE,{"derivedFrom":[makeQuery(id+"F35.boolean.opBoolean","MERGE",FACE,{"derivedFrom":[makeQuery(id+"F25.boolean.opBoolean","MERGE",FACE,{"derivedFrom":[makeQuery(id+"F23.boolean.opBoolean","MERGE",FACE,{"derivedFrom":[makeQuery(id+"F7.opExtrude","CAP_FACE",FACE,{"disambiguationData":[OSD([sQuery(id+"F6.wireOp",EDGE,"E6.bottom"),sQuery(id+"F6.wireOp",EDGE,"E6.top"),sQuery(id+"F6.wireOp",EDGE,"E6.left"),sQuery(id+"F6.wireOp",EDGE,"E6.right")])],"isStart":false}),makeQuery(id+"F7.opExtrude","CAP_FACE",FACE,{"disambiguationData":[OSD([sQuery(id+"F6.wireOp",EDGE,"E9.bottom"),sQuery(id+"F6.wireOp",EDGE,"E9.top"),sQuery(id+"F6.wireOp",EDGE,"E9.left"),sQuery(id+"F6.wireOp",EDGE,"E9.right")])],"isStart":false}),makeQuery(id+"F21.boolean.opBoolean","MERGE",FACE,{"derivedFrom":[makeQuery(id+"F7.opExtrude","CAP_FACE",FACE,{"disambiguationData":[OSD([sQuery(id+"F6.wireOp",EDGE,"E7.bottom"),sQuery(id+"F6.wireOp",EDGE,"E7.top"),sQuery(id+"F6.wireOp",EDGE,"E7.left"),sQuery(id+"F6.wireOp",EDGE,"E7.right")])],"isStart":false}),makeQuery(id+"F7.opExtrude","CAP_FACE",FACE,{"disambiguationData":[OSD([sQuery(id+"F6.wireOp",EDGE,"E8.bottom"),sQuery(id+"F6.wireOp",EDGE,"E8.top"),sQuery(id+"F6.wireOp",EDGE,"E8.left"),sQuery(id+"F6.wireOp",EDGE,"E8.right")])],"isStart":false}),makeQuery(id+"F21.opExtrude","SWEPT_FACE",FACE,{"disambiguationData":[OSD([sQuery(id+"F20.wireOp",EDGE,"E20.bottom")])]})]}),makeQuery(id+"F23.opExtrude","SWEPT_FACE",FACE,{"disambiguationData":[OSD([sQuery(id+"F22.wireOp",EDGE,"E21.bottom")])]}),makeQuery(id+"F23.opExtrude","SWEPT_FACE",FACE,{"disambiguationData":[OSD([sQuery(id+"F22.wireOp",EDGE,"E22.top")])]})]}),makeQuery(id+"F25.opExtrude","SWEPT_FACE",FACE,{"disambiguationData":[OSD([sQuery(id+"F24.wireOp",EDGE,"E23.bottom")])]})]}),makeQuery(id+"F35.opExtrude","SWEPT_FACE",FACE,{"disambiguationData":[OSD([sQuery(id+"F34.wireOp",EDGE,"E32.bottom")])]}),makeQuery(id+"F35.opExtrude","SWEPT_FACE",FACE,{"disambiguationData":[OSD([sQuery(id+"F34.wireOp",EDGE,"E33.top")])]})]}),makeQuery(id+"F37.opExtrude","SWEPT_FACE",FACE,{"disambiguationData":[OSD([sQuery(id+"F36.wireOp",EDGE,"6ef65c90-f17c-4637-9278-1ad8f59648fd.top")])]})]});
            var sketch = newSketch(context, id + "F38", { "sketchPlane" : qUnion([Q0])});
            skLineSegment(sketch, "E37.bottom", {"start": v(-269.64, -173.3) * mm, "end": v(-249.64, -173.3) * mm});
            skLineSegment(sketch, "E37.top", {"start": v(-269.64, -153.3) * mm, "end": v(-249.64, -153.3) * mm});
            skLineSegment(sketch, "E37.left", {"start": v(-269.64, -173.3) * mm, "end": v(-269.64, -153.3) * mm});
            skLineSegment(sketch, "E37.right", {"start": v(-249.64, -173.3) * mm, "end": v(-249.64, -153.3) * mm});
            skLineSegment(sketch, "E38.bottom", {"start": v(-249.64, 126.7) * mm, "end": v(-269.64, 126.7) * mm});
            skLineSegment(sketch, "E38.top", {"start": v(-249.64, 106.7) * mm, "end": v(-269.64, 106.7) * mm});
            skLineSegment(sketch, "E38.left", {"start": v(-249.64, 126.7) * mm, "end": v(-249.64, 106.7) * mm});
            skLineSegment(sketch, "E38.right", {"start": v(-269.64, 126.7) * mm, "end": v(-269.64, 106.7) * mm});
            skLineSegment(sketch, "E39.bottom", {"start": v(195.36, 126.7) * mm, "end": v(175.36, 126.7) * mm});
            skLineSegment(sketch, "E39.top", {"start": v(195.36, 106.7) * mm, "end": v(175.36, 106.7) * mm});
            skLineSegment(sketch, "E39.left", {"start": v(195.36, 126.7) * mm, "end": v(195.36, 106.7) * mm});
            skLineSegment(sketch, "E39.right", {"start": v(175.36, 126.7) * mm, "end": v(175.36, 106.7) * mm});
            skLineSegment(sketch, "E40.bottom", {"start": v(195.36, -153.3) * mm, "end": v(175.36, -153.3) * mm});
            skLineSegment(sketch, "E40.top", {"start": v(195.36, -173.3) * mm, "end": v(175.36, -173.3) * mm});
            skLineSegment(sketch, "E40.left", {"start": v(195.36, -153.3) * mm, "end": v(195.36, -173.3) * mm});
            skLineSegment(sketch, "E40.right", {"start": v(175.36, -153.3) * mm, "end": v(175.36, -173.3) * mm});
            skSolve(sketch);
        }
        {
            var Q0;
            Q0 = qSketchRegion(id + "F38", true);
            extrude(context, id + "F39", {"entities" : qUnion([Q0]), "operationType" : NewBodyOperationType.ADD, "depth" : 410 * mm});
        }
        {
            var Q0;
            Q0=makeQuery(id+"F39.boolean.opBoolean","MERGE",FACE,{"derivedFrom":[makeQuery(id+"F25.opExtrude","SWEPT_FACE",FACE,{"disambiguationData":[OSD([sQuery(id+"F24.wireOp",EDGE,"E23.right")])]}),makeQuery(id+"F39.opExtrude","SWEPT_FACE",FACE,{"disambiguationData":[OSD([sQuery(id+"F38.wireOp",EDGE,"E39.top")])]})]});
            var sketch = newSketch(context, id + "F40", { "sketchPlane" : qUnion([Q0])});
            skLineSegment(sketch, "E41.bottom", {"start": v(175.36, 1770) * mm, "end": v(195.36, 1770) * mm});
            skLineSegment(sketch, "E41.top", {"start": v(175.36, 1750) * mm, "end": v(195.36, 1750) * mm});
            skLineSegment(sketch, "E41.left", {"start": v(175.36, 1770) * mm, "end": v(175.36, 1750) * mm});
            skLineSegment(sketch, "E41.right", {"start": v(195.36, 1770) * mm, "end": v(195.36, 1750) * mm});
            skSolve(sketch);
        }
        {
            var Q0;
            Q0 = qSketchRegion(id + "F40", true);
            extrude(context, id + "F41", {"entities" : qUnion([Q0]), "operationType" : NewBodyOperationType.ADD, "endBound" : BoundingType.UP_TO_NEXT, "depth" : 25 * mm});
        }
        {
            var Q0;
            Q0=makeQuery(id+"F41.boolean.opBoolean","MERGE",FACE,{"derivedFrom":[makeQuery(id+"F39.opExtrude","SWEPT_FACE",FACE,{"disambiguationData":[OSD([sQuery(id+"F38.wireOp",EDGE,"E39.right")])]}),makeQuery(id+"F39.opExtrude","SWEPT_FACE",FACE,{"disambiguationData":[OSD([sQuery(id+"F38.wireOp",EDGE,"E40.right")])]}),makeQuery(id+"F41.opExtrude","SWEPT_FACE",FACE,{"disambiguationData":[OSD([sQuery(id+"F40.wireOp",EDGE,"E41.left")])]})]});
            var sketch = newSketch(context, id + "F42", { "sketchPlane" : qUnion([Q0])});
            skLineSegment(sketch, "E42.bottom", {"start": v(-126.7, 1770) * mm, "end": v(-106.7, 1770) * mm});
            skLineSegment(sketch, "E42.top", {"start": v(-126.7, 1750) * mm, "end": v(-106.7, 1750) * mm});
            skLineSegment(sketch, "E42.left", {"start": v(-126.7, 1770) * mm, "end": v(-126.7, 1750) * mm});
            skLineSegment(sketch, "E42.right", {"start": v(-106.7, 1770) * mm, "end": v(-106.7, 1750) * mm});
            skLineSegment(sketch, "E43.bottom", {"start": v(153.3, 1750) * mm, "end": v(173.3, 1750) * mm});
            skLineSegment(sketch, "E43.top", {"start": v(153.3, 1770) * mm, "end": v(173.3, 1770) * mm});
            skLineSegment(sketch, "E43.left", {"start": v(153.3, 1750) * mm, "end": v(153.3, 1770) * mm});
            skLineSegment(sketch, "E43.right", {"start": v(173.3, 1750) * mm, "end": v(173.3, 1770) * mm});
            skSolve(sketch);
        }
        {
            var Q0;
            Q0 = qSketchRegion(id + "F42", true);
            extrude(context, id + "F43", {"entities" : qUnion([Q0]), "operationType" : NewBodyOperationType.ADD, "endBound" : BoundingType.UP_TO_NEXT, "depth" : 25 * mm});
        }
        {
            var Q0;
            Q0=makeQuery(id+"F43.boolean.opBoolean","MERGE",FACE,{"derivedFrom":[makeQuery(id+"F39.opExtrude","SWEPT_FACE",FACE,{"disambiguationData":[OSD([sQuery(id+"F38.wireOp",EDGE,"E38.top")])]}),makeQuery(id+"F43.opExtrude","SWEPT_FACE",FACE,{"disambiguationData":[OSD([sQuery(id+"F42.wireOp",EDGE,"E42.right")])]})]});
            var sketch = newSketch(context, id + "F44", { "sketchPlane" : qUnion([Q0])});
            skLineSegment(sketch, "E44.bottom", {"start": v(-269.64, 1770) * mm, "end": v(-249.64, 1770) * mm});
            skLineSegment(sketch, "E44.top", {"start": v(-269.64, 1750) * mm, "end": v(-249.64, 1750) * mm});
            skLineSegment(sketch, "E44.left", {"start": v(-269.64, 1770) * mm, "end": v(-269.64, 1750) * mm});
            skLineSegment(sketch, "E44.right", {"start": v(-249.64, 1770) * mm, "end": v(-249.64, 1750) * mm});
            skSolve(sketch);
        }
        {
            var Q0;
            Q0 = qSketchRegion(id + "F44", true);
            extrude(context, id + "F45", {"entities" : qUnion([Q0]), "operationType" : NewBodyOperationType.ADD, "endBound" : BoundingType.UP_TO_NEXT, "depth" : 25 * mm});
        }
        {
            var Q0;
            {var subQ0=sQuery(id+"F6.wireOp",EDGE,"E9.left");var subQ1=makeQuery(id+"F7.opExtrude","SWEPT_FACE",FACE,{"disambiguationData":[OSD([subQ0])]});var subQ2=makeQuery(id+"F11.opExtrude","SWEPT_FACE",FACE,{"disambiguationData":[OSD([sQuery(id+"F10.wireOp",EDGE,"E12.left")])]});var subQ4=sQuery(id+"F6.wireOp",EDGE,"E9.bottom");var subQ5=sQuery(id+"F6.wireOp",EDGE,"E9.top");var subQ6=makeQuery(id+"F1.opExtrude","SWEPT_FACE",FACE,{"disambiguationData":[OSD([sQuery(id+"F0.wireOp",EDGE,"E0.bottom")])]});var subQ13=makeQuery(id+"F23.opExtrude","SWEPT_FACE",FACE,{"disambiguationData":[OSD([sQuery(id+"F22.wireOp",EDGE,"E21.right")])]});Q0=makeQuery(id+"F35.boolean.opBoolean","MERGE",FACE,{"derivedFrom":[makeQuery(id+"F25.boolean.opBoolean","SPLIT",FACE,{"disambiguationData":[TD([subQ6])],"derivedFrom":makeQuery(id+"F23.boolean.opBoolean","MERGE",FACE,{"derivedFrom":[makeQuery(id+"F13.boolean.opBoolean","SPLIT",FACE,{"disambiguationData":[TD([makeQuery(id+"F7.opExtrude","CAP_FACE",FACE,{"disambiguationData":[OSD([subQ4,subQ5,subQ0,sQuery(id+"F6.wireOp",EDGE,"E9.right")])],"isStart":false})])],"derivedFrom":makeQuery(id+"F11.boolean.opBoolean","MERGE",FACE,{"derivedFrom":[subQ1,subQ2]})}),subQ13]})}),makeQuery(id+"F35.opExtrude","SWEPT_FACE",FACE,{"disambiguationData":[OSD([sQuery(id+"F34.wireOp",EDGE,"E34.right")])]})]});}
            var sketch = newSketch(context, id + "F46", { "sketchPlane" : qUnion([Q0])});
            skLineSegment(sketch, "E45.bottom", {"start": v(-186.7, 1310) * mm, "end": v(-166.7, 1310) * mm});
            skLineSegment(sketch, "E45.top", {"start": v(-186.7, 1290) * mm, "end": v(-166.7, 1290) * mm});
            skLineSegment(sketch, "E45.left", {"start": v(-186.7, 1310) * mm, "end": v(-186.7, 1290) * mm});
            skLineSegment(sketch, "E45.right", {"start": v(-166.7, 1310) * mm, "end": v(-166.7, 1290) * mm});
            skSolve(sketch);
        }
        {
            var Q0;
            Q0 = qSketchRegion(id + "F46", true);
            extrude(context, id + "F47", {"entities" : qUnion([Q0]), "operationType" : NewBodyOperationType.ADD, "endBound" : BoundingType.UP_TO_NEXT, "depth" : 25 * mm});
        }
    });
